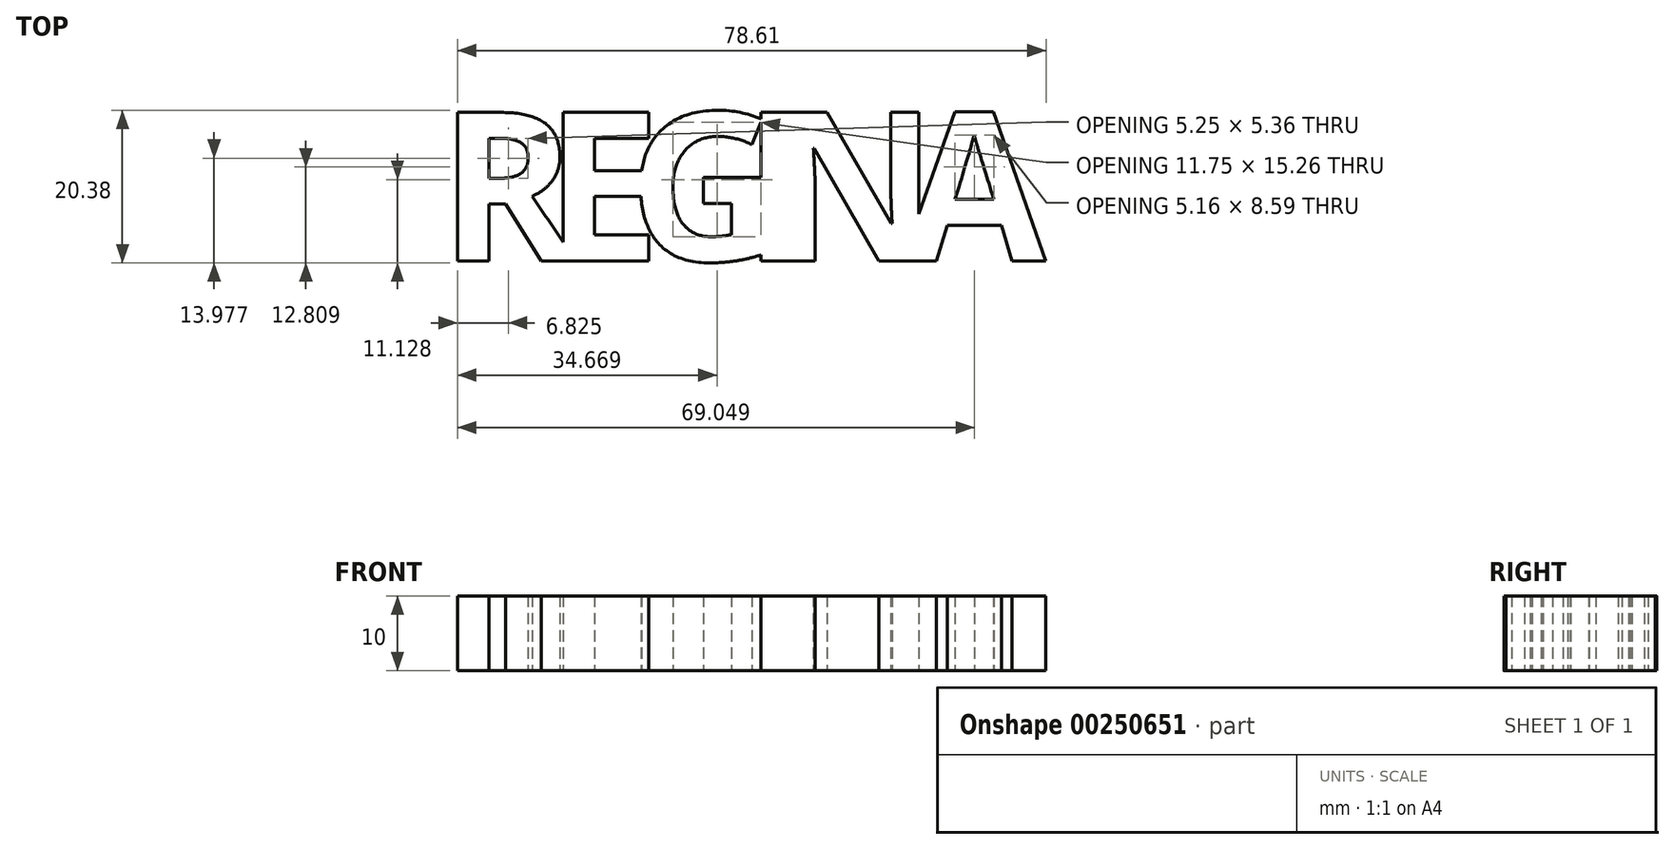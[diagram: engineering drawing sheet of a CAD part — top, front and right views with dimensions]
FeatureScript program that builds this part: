
annotation { "Feature Type Name" : "Feature", "Feature Type Description" : "" }
export const myFeature = defineFeature(function(context is Context, id is Id, definition is map)
    precondition{}
    {
        {
            var Q0;
            Q0=qCreatedBy(makeId("Top.planeOp"),FACE);
            var sketch = newSketch(context, id + "F0", { "sketchPlane" : qUnion([Q0])});
            skText(sketch, "E0", { "text": "R", "fontName": "OpenSans-Bold.ttf"});
            skText(sketch, "E1", { "text": "E", "fontName": "OpenSans-Bold.ttf"});
            skText(sketch, "E2", { "text": "G", "fontName": "OpenSans-Bold.ttf"});
            skText(sketch, "E3", { "text": "I", "fontName": "OpenSans-Bold.ttf"});
            skText(sketch, "E4", { "text": "N", "fontName": "OpenSans-Bold.ttf"});
            skText(sketch, "E5", { "text": "A", "fontName": "OpenSans-Bold.ttf"});
            const initialGuessF0  = {"E0": [-0.04957, 0, 1, 0, 0.02], "E1": [-0.03543, 0, 1, 0, 0.02], "E2": [-0.02422, 0, 1, 0, 0.02], "E3": [-0.00902, 0, 1, 0, 0.02], "E4": [-0.00552, 0, 1, 0, 0.02], "E5": [0.01237, 0, 1, 0, 0.02]};
            skSetInitialGuess(sketch, initialGuessF0);
            skSolve(sketch);
        }
        {
            var Q0;
            Q0 = qSketchRegion(id + "F0", true);
            extrude(context, id + "F1", {"entities" : qUnion([Q0]), "depth" : 10 * mm});
        }
    });
